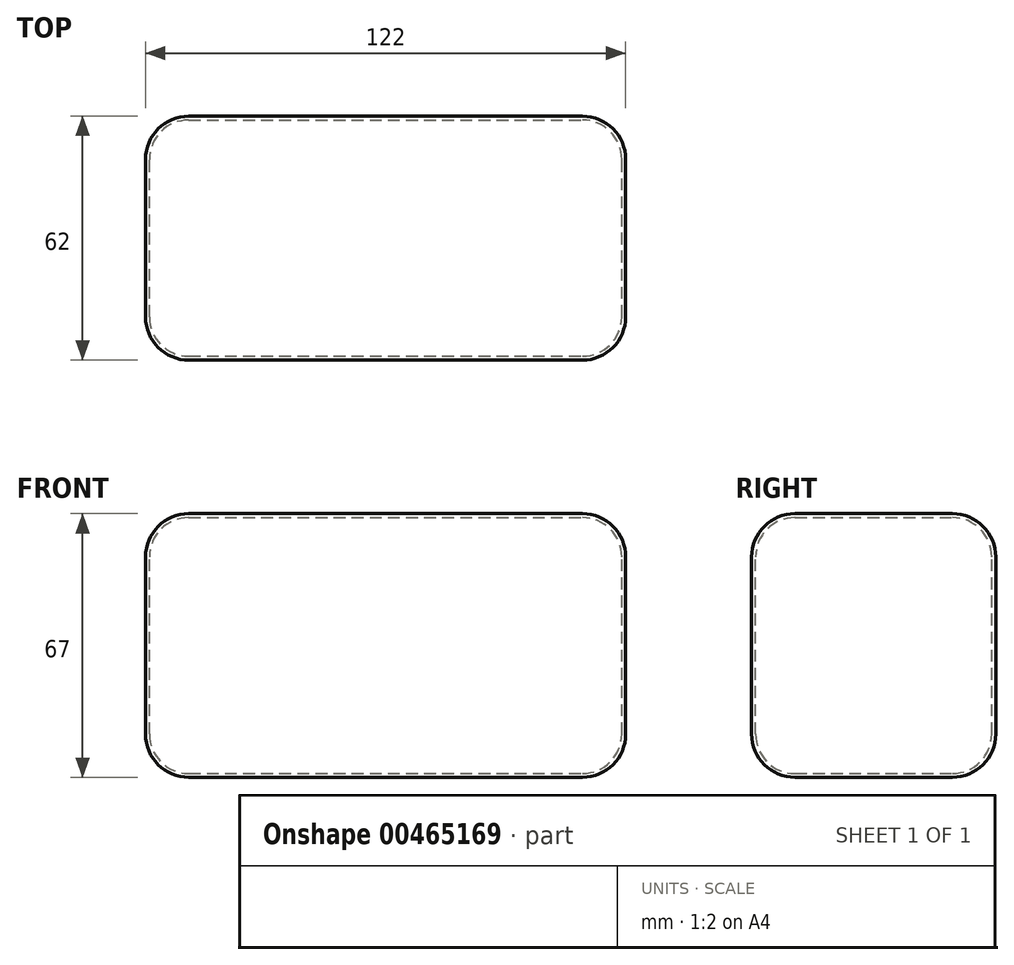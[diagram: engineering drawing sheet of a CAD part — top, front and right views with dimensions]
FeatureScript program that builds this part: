
annotation { "Feature Type Name" : "Feature", "Feature Type Description" : "" }
export const myFeature = defineFeature(function(context is Context, id is Id, definition is map)
    precondition{}
    {
        {
            var Q0;
            Q0=qCreatedBy(makeId("Front.planeOp"),FACE);
            var sketch = newSketch(context, id + "F0", { "sketchPlane" : qUnion([Q0])});
            skLineSegment(sketch, "E0.bottom", {"start": v(-60.1, -32.4) * mm, "end": v(59.9, -32.4) * mm});
            skLineSegment(sketch, "E0.top", {"start": v(-60.1, 32.6) * mm, "end": v(59.9, 32.6) * mm});
            skLineSegment(sketch, "E0.left", {"start": v(-60.1, -32.4) * mm, "end": v(-60.1, 32.6) * mm});
            skLineSegment(sketch, "E0.right", {"start": v(59.9, -32.4) * mm, "end": v(59.9, 32.6) * mm});
            skSolve(sketch);
        }
        {
            var Q0;
            Q0=makeQuery(id+"F0.imprint","IMPRINT",FACE,{"disambiguationData":[TD([[makeQuery(id+"F0.imprint","IMPRINT",EDGE,{"derivedFrom":sQuery(id+"F0.wireOp",EDGE,"E0.bottom")}),1.0]])]});
            extrude(context, id + "F1", {"entities" : qUnion([Q0]), "endBound" : BoundingType.SYMMETRIC, "depth" : 60 * mm});
        }
        {
            var Q0;
            Q0=makeQuery(id+"F1.opExtrude","CAP_EDGE",EDGE,{"disambiguationData":[OSD([sQuery(id+"F0.wireOp",EDGE,"E0.bottom")])],"isStart":false});
            var Q1;
            Q1=makeQuery(id+"F1.opExtrude","SWEPT_EDGE",EDGE,{"disambiguationData":[OSD([sQuery(id+"F0.wireOp",EDGE,"E0.bottom"),sQuery(id+"F0.wireOp",EDGE,"E0.right")])]});
            var Q2;
            Q2=makeQuery(id+"F1.opExtrude","CAP_EDGE",EDGE,{"disambiguationData":[OSD([sQuery(id+"F0.wireOp",EDGE,"E0.bottom")])],"isStart":true});
            var Q3;
            Q3=makeQuery(id+"F1.opExtrude","SWEPT_EDGE",EDGE,{"disambiguationData":[OSD([sQuery(id+"F0.wireOp",EDGE,"E0.bottom"),sQuery(id+"F0.wireOp",EDGE,"E0.left")])]});
            var Q4;
            Q4=makeQuery(id+"F1.opExtrude","CAP_EDGE",EDGE,{"disambiguationData":[OSD([sQuery(id+"F0.wireOp",EDGE,"E0.top")])],"isStart":false});
            var Q5;
            Q5=makeQuery(id+"F1.opExtrude","SWEPT_EDGE",EDGE,{"disambiguationData":[OSD([sQuery(id+"F0.wireOp",EDGE,"E0.top"),sQuery(id+"F0.wireOp",EDGE,"E0.right")])]});
            var Q6;
            Q6=makeQuery(id+"F1.opExtrude","SWEPT_EDGE",EDGE,{"disambiguationData":[OSD([sQuery(id+"F0.wireOp",EDGE,"E0.top"),sQuery(id+"F0.wireOp",EDGE,"E0.left")])]});
            var Q7;
            Q7=makeQuery(id+"F1.opExtrude","CAP_EDGE",EDGE,{"disambiguationData":[OSD([sQuery(id+"F0.wireOp",EDGE,"E0.top")])],"isStart":true});
            var Q8;
            Q8=makeQuery(id+"F1.opExtrude","CAP_EDGE",EDGE,{"disambiguationData":[OSD([sQuery(id+"F0.wireOp",EDGE,"E0.left")])],"isStart":true});
            var Q9;
            Q9=makeQuery(id+"F1.opExtrude","CAP_EDGE",EDGE,{"disambiguationData":[OSD([sQuery(id+"F0.wireOp",EDGE,"E0.left")])],"isStart":false});
            var Q10;
            Q10=makeQuery(id+"F1.opExtrude","CAP_EDGE",EDGE,{"disambiguationData":[OSD([sQuery(id+"F0.wireOp",EDGE,"E0.right")])],"isStart":false});
            var Q11;
            Q11=makeQuery(id+"F1.opExtrude","CAP_EDGE",EDGE,{"disambiguationData":[OSD([sQuery(id+"F0.wireOp",EDGE,"E0.right")])],"isStart":true});
            fillet(context, id + "F2", {"entities" : qUnion([Q0, Q1, Q2, Q3, Q4, Q5, Q6, Q7, Q8, Q9, Q10, Q11]), "radius" : 10 * mm, "tangentPropagation" : true, "allowEdgeOverflow" : false});
        }
        {
            var Q0;
            Q0=makeQuery(id+"F1.opExtrude","CAP_FACE",FACE,{"disambiguationData":[OSD([sQuery(id+"F0.wireOp",EDGE,"E0.bottom"),sQuery(id+"F0.wireOp",EDGE,"E0.top"),sQuery(id+"F0.wireOp",EDGE,"E0.left"),sQuery(id+"F0.wireOp",EDGE,"E0.right")])],"isStart":false});
            var sketch = newSketch(context, id + "F3", { "sketchPlane" : qUnion([Q0])});
            skPoint(sketch, "E1.oppositeSnap0", {"position": v(49.9, 0.1) * mm});
            skLineSegment(sketch, "E1.bottom", {"start": v(-77.57, 88.4) * mm, "end": v(80.68, 88.4) * mm});
            skLineSegment(sketch, "E1.top", {"start": v(-77.57, 0.1) * mm, "end": v(80.68, 0.1) * mm});
            skLineSegment(sketch, "E1.left", {"start": v(-77.57, 88.4) * mm, "end": v(-77.57, 0.1) * mm});
            skLineSegment(sketch, "E1.right", {"start": v(80.68, 88.4) * mm, "end": v(80.68, 0.1) * mm});
            skSolve(sketch);
        }
        {
            var Q0;
            Q0=qSketchRegion(id+"F3",true);
            extrude(context, id + "F4", {"entities" : qUnion([Q0]), "operationType" : NewBodyOperationType.REMOVE, "oppositeDirection" : true, "depth" : 60 * mm});
        }
        {
            var Q0;
            Q0=makeQuery(id+"F4.boolean.opBoolean","COPY",FACE,{"derivedFrom":makeQuery(id+"F4.opExtrude","SWEPT_FACE",FACE,{"disambiguationData":[OSD([sQuery(id+"F3.wireOp",EDGE,"E1.top")])]})});
            shell(context, id + "F5", {"entities" : qUnion([Q0]), "thickness" : 1 * mm, "oppositeDirection" : true});
        }
        {
            var Q0;
            Q0=makeQuery(id+"F1.opExtrude","SWEPT_BODY",BODY,{"disambiguationData":[OSD([sQuery(id+"F0.wireOp",EDGE,"E0.bottom"),sQuery(id+"F0.wireOp",EDGE,"E0.top"),sQuery(id+"F0.wireOp",EDGE,"E0.left"),sQuery(id+"F0.wireOp",EDGE,"E0.right")])]});
            var Q1;
            Q1=makeQuery(id+"F4.boolean.opBoolean","COPY",FACE,{"derivedFrom":makeQuery(id+"F4.opExtrude","SWEPT_FACE",FACE,{"disambiguationData":[OSD([sQuery(id+"F3.wireOp",EDGE,"E1.top")])]})});
            mirror(context, id + "F6", {"operationType" : NewBodyOperationType.ADD, "entities" : qUnion([Q0]), "mirrorPlane" : qUnion([Q1])});
        }
    });
